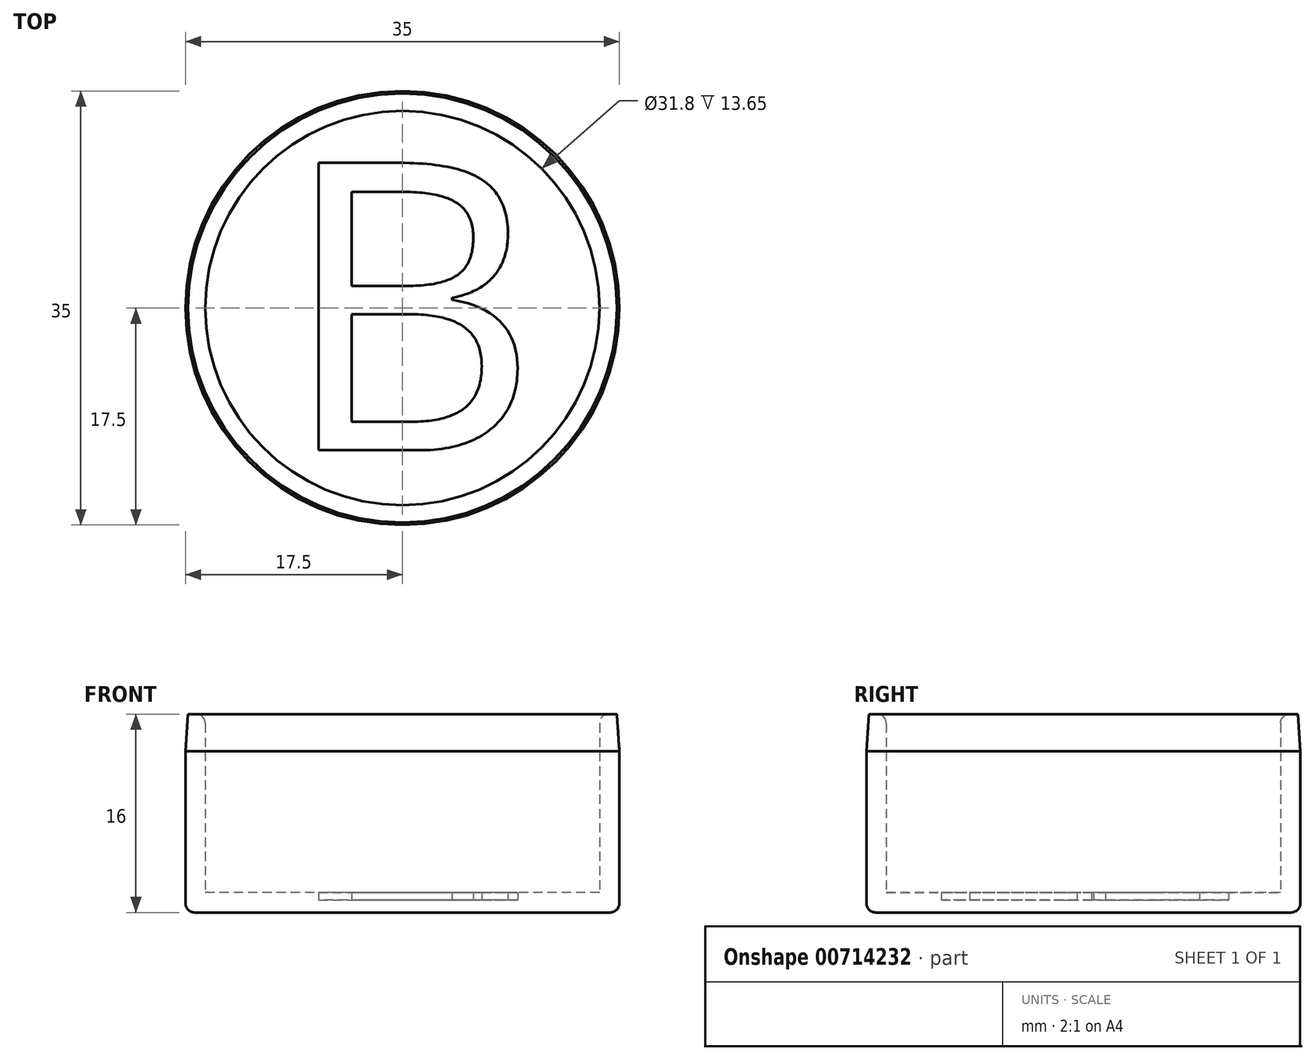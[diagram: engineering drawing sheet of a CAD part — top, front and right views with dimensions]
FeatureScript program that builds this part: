
annotation { "Feature Type Name" : "Feature", "Feature Type Description" : "" }
export const myFeature = defineFeature(function(context is Context, id is Id, definition is map)
    precondition{}
    {
        {
            var Q0;
            Q0=qCreatedBy(makeId("Top.planeOp"),FACE);
            var sketch = newSketch(context, id + "F0", { "sketchPlane" : qUnion([Q0])});
            skCircle(sketch, "E0", {"center": v(0, 0) * mm, "radius": 17.5 * mm});
            skCircle(sketch, "E1", {"center": v(0, 0) * mm, "radius": 15.9 * mm});
            skText(sketch, "E2", { "text": "B", "fontName": "OpenSans-Regular.ttf"});
            const initialGuessF0  = {"E2": [-0.00996, -0.01147, 1, 0, 0.02338]};
            skSetInitialGuess(sketch, initialGuessF0);
            skSolve(sketch);
        }
        {
            var Q0;
            Q0=makeQuery(id+"F0.imprint","IMPRINT",FACE,{"disambiguationData":[TD([[makeQuery(id+"F0.imprint","IMPRINT",EDGE,{"derivedFrom":sQuery(id+"F0.wireOp",EDGE,"E1")}),1.0]])]});
            extrude(context, id + "F1", {"entities" : qUnion([Q0]), "depth" : 1.6 * mm, "offsetDistance" : 25 * mm});
        }
        {
            var Q0;
            Q0 = qSketchRegion(id + "F0", true);
            extrude(context, id + "F2", {"entities" : qUnion([Q0]), "operationType" : NewBodyOperationType.ADD, "depth" : 16 * mm, "offsetDistance" : 25 * mm});
        }
        {
            var Q0;
            Q0=makeQuery(id+"F2.opExtrude","CAP_EDGE",EDGE,{"disambiguationData":[OSD([sQuery(id+"F0.wireOp",EDGE,"E0")])],"isStart":false});
            chamfer(context, id + "F3", {"entities" : qUnion([Q0]), "chamferType" : ChamferType.TWO_OFFSETS, "width1" : 0.2 * mm, "oppositeDirection" : false, "width2" : 3 * mm, "tangentPropagation" : true});
        }
        {
            var Q0;
            Q0=makeQuery(id+"F2.opExtrude","CAP_EDGE",EDGE,{"disambiguationData":[OSD([sQuery(id+"F0.wireOp",EDGE,"E0")])],"isStart":true});
            var Q1;
            Q1=makeQuery(id+"F2.opExtrude","CAP_EDGE",EDGE,{"disambiguationData":[OSD([sQuery(id+"F0.wireOp",EDGE,"E1")])],"isStart":false});
            fillet(context, id + "F4", {"entities" : qUnion([Q0, Q1]), "radius" : 0.75 * mm, "tangentPropagation" : true, "allowEdgeOverflow" : false});
        }
        {
            var Q0;
            Q0=makeQuery(id+"F0.imprint","IMPRINT",FACE,{"disambiguationData":[TD([[makeQuery(id+"F0.imprint","IMPRINT",EDGE,{"derivedFrom":sQuery(id+"F0.wireOp",EDGE,"E2.sketch_text.stroke-0")}),-1.0]])]});
            extrude(context, id + "F5", {"entities" : qUnion([Q0]), "operationType" : NewBodyOperationType.ADD, "depth" : 1 * mm, "offsetDistance" : 25 * mm});
        }
        {
            var Q0;
            Q0=makeQuery(id+"F0.imprint","IMPRINT",FACE,{"disambiguationData":[TD([[makeQuery(id+"F0.imprint","IMPRINT",EDGE,{"derivedFrom":sQuery(id+"F0.wireOp",EDGE,"E2.sketch_text.stroke-11")}),1.0]])]});
            var Q1;
            Q1=makeQuery(id+"F0.imprint","IMPRINT",FACE,{"disambiguationData":[TD([[makeQuery(id+"F0.imprint","IMPRINT",EDGE,{"derivedFrom":sQuery(id+"F0.wireOp",EDGE,"E2.sketch_text.stroke-18")}),1.0]])]});
            extrude(context, id + "F6", {"entities" : qUnion([Q0, Q1]), "operationType" : NewBodyOperationType.ADD, "depth" : 1.6 * mm, "offsetDistance" : 25 * mm});
        }
    });
